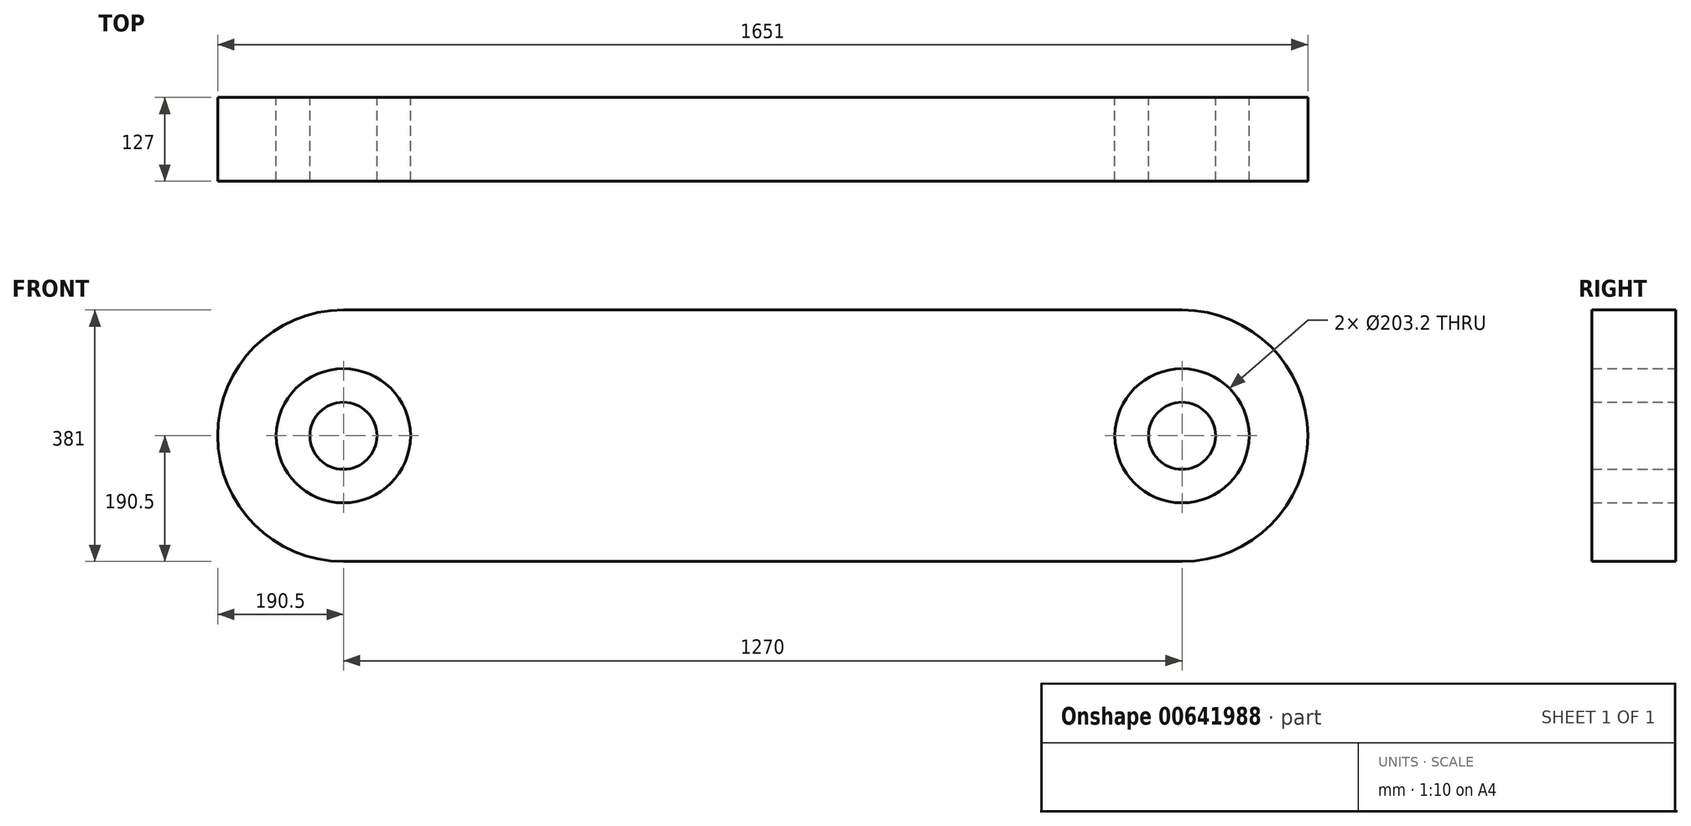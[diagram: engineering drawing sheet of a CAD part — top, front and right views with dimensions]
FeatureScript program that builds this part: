
annotation { "Feature Type Name" : "Feature", "Feature Type Description" : "" }
export const myFeature = defineFeature(function(context is Context, id is Id, definition is map)
    precondition{}
    {
        {
            var Q0;
            Q0=qCreatedBy(makeId("Front.planeOp"),FACE);
            var sketch = newSketch(context, id + "F0", { "sketchPlane" : qUnion([Q0])});
            skArc(sketch, "E0", {"start": v(0, 190.5) * mm, "mid": v(-190.5, 0) * mm, "end": v(0, -190.5) * mm});
            skArc(sketch, "E1", {"start": v(1270, -190.5) * mm, "mid": v(1460.5, 0) * mm, "end": v(1270, 190.5) * mm});
            skLineSegment(sketch, "E2", {"start": v(0, 190.5) * mm, "end": v(1270, 190.5) * mm});
            skLineSegment(sketch, "E3", {"start": v(0, -190.5) * mm, "end": v(1270, -190.5) * mm});
            skCircle(sketch, "E4", {"center": v(0, 0) * mm, "radius": 101.6 * mm});
            skCircle(sketch, "E5", {"center": v(1270, 0) * mm, "radius": 101.6 * mm});
            skCircle(sketch, "E6", {"center": v(0, 0) * mm, "radius": 50.8 * mm});
            skCircle(sketch, "E7", {"center": v(1270, 0) * mm, "radius": 50.8 * mm});
            skSolve(sketch);
        }
        {
            var Q0;
            Q0=makeQuery(id+"F0.imprint","IMPRINT",FACE,{"disambiguationData":[TD([[makeQuery(id+"F0.imprint","IMPRINT",EDGE,{"derivedFrom":sQuery(id+"F0.wireOp",EDGE,"E0")}),1.0]])]});
            var Q1;
            Q1=makeQuery(id+"F0.imprint","IMPRINT",FACE,{"disambiguationData":[TD([[makeQuery(id+"F0.imprint","IMPRINT",EDGE,{"derivedFrom":sQuery(id+"F0.wireOp",EDGE,"E6")}),1.0]])]});
            var Q2;
            Q2=makeQuery(id+"F0.imprint","IMPRINT",FACE,{"disambiguationData":[TD([[makeQuery(id+"F0.imprint","IMPRINT",EDGE,{"derivedFrom":sQuery(id+"F0.wireOp",EDGE,"E7")}),1.0]])]});
            extrude(context, id + "F1", {"entities" : qUnion([Q0, Q1, Q2]), "depth" : 127 * mm, "offsetDistance" : 25.4 * mm});
        }
    });
